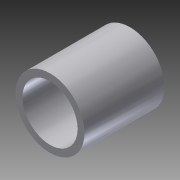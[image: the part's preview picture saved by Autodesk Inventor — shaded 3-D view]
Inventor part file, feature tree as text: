
AUTODESK INVENTOR PART (.ipt)
format: ipt  version: 2013 (Build 170138000, 138)  size: 84,480 bytes
history: native  units: in
note: dims shown in document units (in); Inventor stores cm internally (conversion verified against a paired STEP export)
features: extrude x1, sketch x1
ambient origin geometry x8: Origin, YZ Plane, XZ Plane, XY Plane, X Axis, Y Axis, Z Axis, Center Point
bodies: Solid1 (feature_tree)
feature tree (2):
  extrude  "Extrusion1"  Depth=0.5in
  sketch  "Sketch1"  dims[d0=0.625in d1=0.5in d2=0.725in d3=0.0in]
